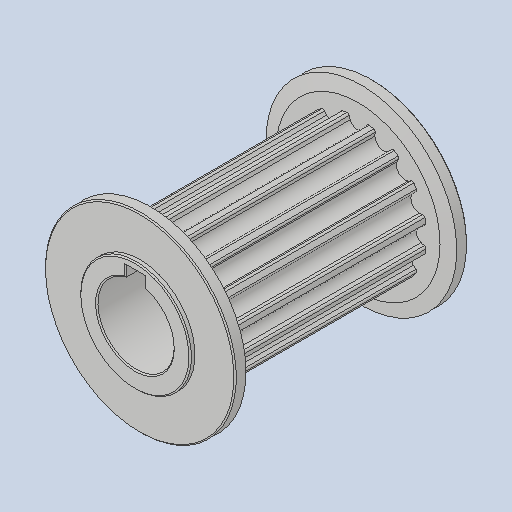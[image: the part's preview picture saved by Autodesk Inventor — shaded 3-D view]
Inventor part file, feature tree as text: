
AUTODESK INVENTOR PART (.ipt)
format: ipt  version: 2023.3 (Build 273359000, 359)  size: 266,240 bytes
history: native  units: in
note: dims shown in document units (in); Inventor stores cm internally (conversion verified against a paired STEP export)
features: chamfer x1
ambient origin geometry x8: Origin, YZ Plane, XZ Plane, XY Plane, X Axis, Y Axis, Z Axis, Center Point
bodies: Solid1 (feature_tree)
feature tree (1):
  chamfer  "Chamfer2"  [1 undecoded]
note: 1 required parameter value undecoded (feature->parameter linkage not recoverable at this tier; creation-order binding heuristic only, values carry confidence <= 0.55)
